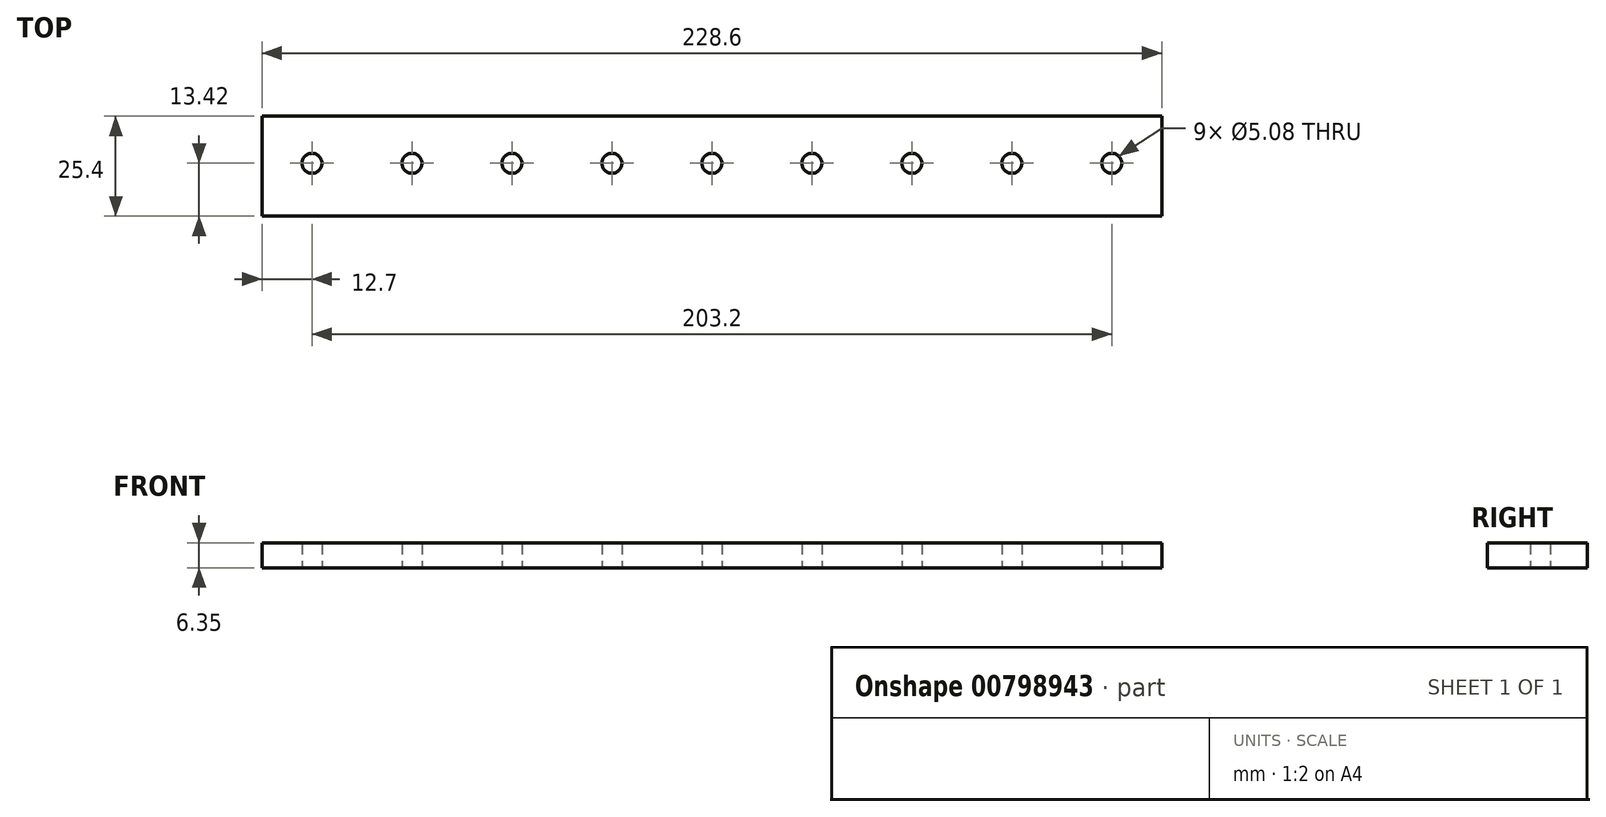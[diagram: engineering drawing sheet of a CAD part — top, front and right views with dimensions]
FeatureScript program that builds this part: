
annotation { "Feature Type Name" : "Feature", "Feature Type Description" : "" }
export const myFeature = defineFeature(function(context is Context, id is Id, definition is map)
    precondition{}
    {
        {
            var Q0;
            Q0=qCreatedBy(makeId("Top.planeOp"),FACE);
            var sketch = newSketch(context, id + "F0", { "sketchPlane" : qUnion([Q0])});
            skLineSegment(sketch, "E0.bottom", {"start": v(0, 11.98) * mm, "end": v(228.6, 11.98) * mm});
            skLineSegment(sketch, "E0.top", {"start": v(0, -13.42) * mm, "end": v(228.6, -13.42) * mm});
            skLineSegment(sketch, "E0.left", {"start": v(0, 11.98) * mm, "end": v(0, -13.42) * mm});
            skLineSegment(sketch, "E0.right", {"start": v(228.6, 11.98) * mm, "end": v(228.6, -13.42) * mm});
            skCircle(sketch, "E1", {"center": v(12.7, 0) * mm, "radius": 2.54 * mm});
            skCircle(sketch, "E2", {"center": v(38.1, 0) * mm, "radius": 2.54 * mm});
            skCircle(sketch, "E3", {"center": v(63.5, 0) * mm, "radius": 2.54 * mm});
            skCircle(sketch, "E4", {"center": v(88.9, 0) * mm, "radius": 2.54 * mm});
            skCircle(sketch, "E5", {"center": v(114.3, 0) * mm, "radius": 2.54 * mm});
            skCircle(sketch, "E6", {"center": v(139.7, 0) * mm, "radius": 2.54 * mm});
            skCircle(sketch, "E7", {"center": v(165.1, 0) * mm, "radius": 2.54 * mm});
            skCircle(sketch, "E8", {"center": v(190.5, 0) * mm, "radius": 2.54 * mm});
            skCircle(sketch, "E9", {"center": v(215.9, 0) * mm, "radius": 2.54 * mm});
            skSolve(sketch);
        }
        {
            var Q0;
            Q0 = qSketchRegion(id + "F0", true);
            extrude(context, id + "F1", {"entities" : qUnion([Q0]), "depth" : 6.35 * mm, "offsetDistance" : 25.4 * mm});
        }
    });
